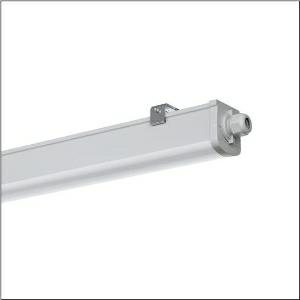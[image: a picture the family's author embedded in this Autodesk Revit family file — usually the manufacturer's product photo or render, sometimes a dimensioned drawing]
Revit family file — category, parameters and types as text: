
# Revit family: monsun_r__31_51fa20dk430b_aae0
name_source: partatom
category: Lighting Fixtures
units: mm (PartAtom-declared; Revit-internal decimal feet)

## family parameters
Cut with Voids When Loaded = No
Host = Face
Light Source = No
Part Type = Normal
Room Calculation Point = No
Round Connector Dimension = Use Diameter
Shared = No

## types (1)
- Monsun® 31 (1 x LED, 3000 lm, 22 W, 4000K)
    Apparent Load = 22 VA
    CIE Flux Codes = 42 72 91 92 100
    Color Rendering = 80
    Color Temperature = 4000K
    Default Elevation = 1800 mm
    Description = Monsun® 31, damp-proof luminaire, primary optical cover: diffuser, of PC, frosted, light emission: direct distribution, primary light characteristic: symmetric, installation type: surface-mounted, LED, rated luminous flux: 3.000lm, luminous efficacy: 136lm/W, light colour: 840, colour temperature: 4000K, control gear: DALI 2, with terminal, 5+1-pole, max. 2.5mm², through-wiring: 3x 2.5mm² + 3x 1.5mm², mains connection: 220..240V, AC, 50/60Hz, rated input power: 22W, housing, luminaire housing, of PC, light grey (RAL 7035), length: 1.158mm, width: 68mm, height: 76mm, protection rating (complete): IP66, insulation class (complete): insulation class II (safety insulation), certification: CE, ENEC, UKCA, protection symbol: D, impact resistance: IK08, permissible operating ambient temperature: -20..+40°C, corresponds to IFS (International Featured Standards) requirements for safety and quality in the food industry, contact your sales advisor before using the luminaires in applications with unclear chemical exposure, large temperature fluctuations or condensation-forming humidity, packaging unit: 1 piece
    Height = 77 mm
    Lamp = 1 x LED
    Lamp Light Flux = 3000 lm
    Lamp Power = 22 W
    Lamp count = 1
    Length = 1218 mm
    Luminous efficacy = 136 lm/W
    Manufacturer = Siteco
    ModVariant = No
    Model = 51FA20DK430B
    Mounting Place = Ceiling
    Mounting Type = Surface mounted
    Number of Poles = 1
    OnlyDefault = Yes
    Power Factor = 1
    Product Name = Monsun® 31
    Product group = damp-proof luminaire
    ProductGroupID = 301
    Protection Class = Protection class II
    Protection Degree = IP 66
    RLX_Detail_Level = 1
    RLX_Emergency_Light_Flux = 0 lm
    RLX_Emergency_Type = 0
    RLX_Emergency_Type_DB = No
    RlxData = <blob elided: 32761 chars, md5=a70c14e9>
    Socket = socket
    Standby Power = 0 W
    System Light Flux = 3000 lm
    System Power = 22 W
    Type Comments = Product without accessories
    Type Image = l_1006174.jpg
    URL = http://relux.com
    VarID = ---
    Voltage = 0 V
    Weight = 0.00 kg
    Width = 69 mm

## geometry (parser evidence)
native form markers: Blend x4, Sweep x11
no freeform markers — native parametric forms only
